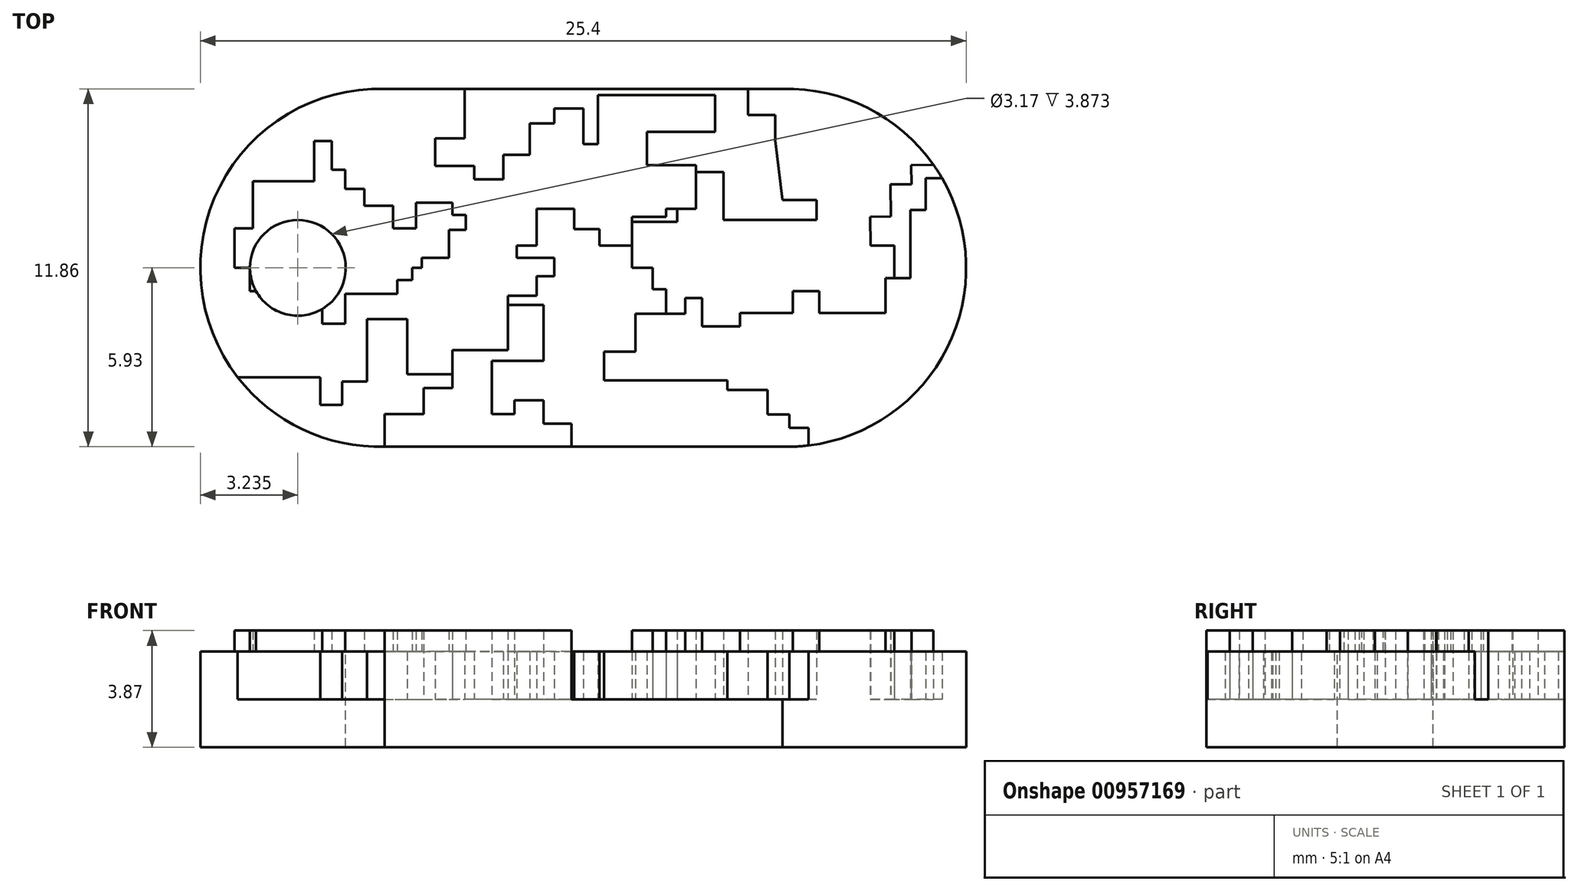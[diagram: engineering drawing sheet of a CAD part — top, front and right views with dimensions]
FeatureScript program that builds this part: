
annotation { "Feature Type Name" : "Feature", "Feature Type Description" : "" }
export const myFeature = defineFeature(function(context is Context, id is Id, definition is map)
    precondition{}
    {
        {
            var Q0;
            Q0=qCreatedBy(makeId("Top.planeOp"),FACE);
            var sketch = newSketch(context, id + "F0", { "sketchPlane" : qUnion([Q0])});
            skLineSegment(sketch, "E0.bottom", {"start": v(6.6, 5.93) * mm, "end": v(-6.6, 5.93) * mm});
            skLineSegment(sketch, "E0.top", {"start": v(6.6, -5.93) * mm, "end": v(-6.6, -5.93) * mm});
            skLineSegment(sketch, "E0.left", {"start": v(6.6, 5.93) * mm, "end": v(6.6, -5.93) * mm});
            skLineSegment(sketch, "E0.right", {"start": v(-6.6, 5.93) * mm, "end": v(-6.6, -5.93) * mm});
            skPoint(sketch, "E0.middle", {"position": v(0, 0) * mm});
            skCircle(sketch, "E1", {"center": v(6.76, 0) * mm, "radius": 5.93 * mm});
            skPoint(sketch, "E1.third.point", {"position": v(11.72, -3.25) * mm});
            skCircle(sketch, "E2", {"center": v(-6.78, 0) * mm, "radius": 5.93 * mm});
            skPoint(sketch, "E2.third.point", {"position": v(-6.95, -5.93) * mm});
            skPoint(sketch, "E3", {"position": v(-12.7, 0) * mm});
            skPoint(sketch, "E4", {"position": v(12.7, 0) * mm});
            skSolve(sketch);
        }
        {
            var Q0;
            {var subQ0=sQuery(id+"F0.wireOp",EDGE,"E0.right");Q0=makeQuery(id+"F0.imprint","IMPRINT",FACE,{"disambiguationData":[TD([[makeQuery(id+"F0.imprint","IMPRINT",EDGE,{"derivedFrom":subQ0}),-1.0]])]});}
            var Q1;
            {var subQ0=sQuery(id+"F0.wireOp",EDGE,"E0.bottom");Q1=makeQuery(id+"F0.imprint","IMPRINT",FACE,{"disambiguationData":[TD([[makeQuery(id+"F0.imprint","IMPRINT",EDGE,{"derivedFrom":subQ0}),1.0]])]});}
            var Q2;
            {var subQ0=sQuery(id+"F0.wireOp",EDGE,"E0.right");Q2=makeQuery(id+"F0.imprint","IMPRINT",FACE,{"disambiguationData":[TD([[makeQuery(id+"F0.imprint","IMPRINT",EDGE,{"derivedFrom":subQ0}),1.0]])]});}
            var Q3;
            {var subQ0=sQuery(id+"F0.wireOp",EDGE,"E0.left");Q3=makeQuery(id+"F0.imprint","IMPRINT",FACE,{"disambiguationData":[TD([[makeQuery(id+"F0.imprint","IMPRINT",EDGE,{"derivedFrom":subQ0}),-1.0]])]});}
            var Q4;
            {var subQ0=sQuery(id+"F0.wireOp",EDGE,"E0.left");Q4=makeQuery(id+"F0.imprint","IMPRINT",FACE,{"disambiguationData":[TD([[makeQuery(id+"F0.imprint","IMPRINT",EDGE,{"derivedFrom":subQ0}),1.0]])]});}
            extrude(context, id + "F1", {"entities" : qUnion([Q0, Q1, Q2, Q3, Q4]), "depth" : 1.59 * mm, "offsetDistance" : 25.4 * mm});
        }
        {
            var Q0;
            Q0=makeQuery(id+"F1.opExtrude","CAP_FACE",FACE,{"disambiguationData":[OSD([sQuery(id+"F0.wireOp",EDGE,"E0.bottom"),sQuery(id+"F0.wireOp",EDGE,"E0.top"),sQuery(id+"F0.wireOp",EDGE,"E1"),sQuery(id+"F0.wireOp",EDGE,"E2")])],"isStart":false});
            var sketch = newSketch(context, id + "F2", { "sketchPlane" : qUnion([Q0])});
            skLineSegment(sketch, "E5", {"start": v(-11.47, -3.63) * mm, "end": v(-8.73, -3.63) * mm});
            skLineSegment(sketch, "E6", {"start": v(-8.73, -3.63) * mm, "end": v(-8.73, -4.54) * mm});
            skLineSegment(sketch, "E7", {"start": v(-8.73, -4.54) * mm, "end": v(-8.01, -4.54) * mm});
            skLineSegment(sketch, "E8", {"start": v(-8.01, -4.54) * mm, "end": v(-8.01, -3.77) * mm});
            skLineSegment(sketch, "E9", {"start": v(-8.01, -3.77) * mm, "end": v(-7.18, -3.77) * mm});
            skLineSegment(sketch, "E10", {"start": v(-7.18, -3.77) * mm, "end": v(-7.18, -1.7) * mm});
            skLineSegment(sketch, "E11", {"start": v(-7.18, -1.7) * mm, "end": v(-5.84, -1.7) * mm});
            skLineSegment(sketch, "E12", {"start": v(-5.84, -1.7) * mm, "end": v(-5.84, -3.53) * mm});
            skLineSegment(sketch, "E13", {"start": v(-5.84, -3.53) * mm, "end": v(-4.35, -3.53) * mm});
            skLineSegment(sketch, "E14", {"start": v(-4.35, -3.53) * mm, "end": v(-4.35, -2.74) * mm});
            skLineSegment(sketch, "E15", {"start": v(-4.35, -2.74) * mm, "end": v(-2.5, -2.74) * mm});
            skLineSegment(sketch, "E16", {"start": v(-2.5, -2.74) * mm, "end": v(-2.5, -0.93) * mm});
            skLineSegment(sketch, "E17", {"start": v(-2.5, -0.93) * mm, "end": v(-1.55, -0.93) * mm});
            skLineSegment(sketch, "E18", {"start": v(-1.55, -0.93) * mm, "end": v(-1.55, -0.27) * mm});
            skLineSegment(sketch, "E19", {"start": v(-1.55, -0.27) * mm, "end": v(-0.97, -0.27) * mm});
            skLineSegment(sketch, "E20", {"start": v(-0.97, -0.27) * mm, "end": v(-0.97, 0.34) * mm});
            skLineSegment(sketch, "E21", {"start": v(-0.97, 0.34) * mm, "end": v(-2.2, 0.34) * mm});
            skLineSegment(sketch, "E22", {"start": v(-2.2, 0.34) * mm, "end": v(-2.2, 0.74) * mm});
            skLineSegment(sketch, "E23", {"start": v(-2.2, 0.74) * mm, "end": v(-1.55, 0.74) * mm});
            skLineSegment(sketch, "E24", {"start": v(-1.55, 0.74) * mm, "end": v(-1.55, 1.96) * mm});
            skLineSegment(sketch, "E25", {"start": v(-1.55, 1.96) * mm, "end": v(-0.31, 1.96) * mm});
            skLineSegment(sketch, "E26", {"start": v(-0.31, 1.96) * mm, "end": v(-0.31, 1.28) * mm});
            skLineSegment(sketch, "E27", {"start": v(-0.31, 1.28) * mm, "end": v(0.52, 1.28) * mm});
            skLineSegment(sketch, "E28", {"start": v(0.52, 1.28) * mm, "end": v(0.52, 0.74) * mm});
            skLineSegment(sketch, "E29", {"start": v(0.52, 0.74) * mm, "end": v(1.6, 0.74) * mm});
            skLineSegment(sketch, "E30", {"start": v(1.6, 0.74) * mm, "end": v(1.6, 1.7) * mm});
            skLineSegment(sketch, "E31", {"start": v(1.6, 1.7) * mm, "end": v(2.74, 1.7) * mm});
            skLineSegment(sketch, "E32", {"start": v(2.74, 1.7) * mm, "end": v(2.74, 1.96) * mm});
            skLineSegment(sketch, "E33", {"start": v(2.74, 1.96) * mm, "end": v(3.73, 1.96) * mm});
            skLineSegment(sketch, "E34", {"start": v(3.73, 1.96) * mm, "end": v(3.73, 3.4) * mm});
            skLineSegment(sketch, "E35", {"start": v(3.73, 3.4) * mm, "end": v(2.1, 3.4) * mm});
            skLineSegment(sketch, "E36", {"start": v(2.1, 3.4) * mm, "end": v(2.1, 4.51) * mm});
            skLineSegment(sketch, "E37", {"start": v(2.1, 4.51) * mm, "end": v(4.36, 4.51) * mm});
            skLineSegment(sketch, "E38", {"start": v(4.36, 4.51) * mm, "end": v(4.36, 5.73) * mm});
            skLineSegment(sketch, "E39", {"start": v(4.36, 5.73) * mm, "end": v(0.48, 5.73) * mm});
            skLineSegment(sketch, "E40", {"start": v(0.48, 5.73) * mm, "end": v(0.48, 4.1) * mm});
            skLineSegment(sketch, "E41", {"start": v(0.48, 4.1) * mm, "end": v(0, 4.1) * mm});
            skLineSegment(sketch, "E42", {"start": v(0, 4.1) * mm, "end": v(0, 5.28) * mm});
            skLineSegment(sketch, "E43", {"start": v(0, 5.28) * mm, "end": v(-0.97, 5.28) * mm});
            skLineSegment(sketch, "E44", {"start": v(-0.97, 5.28) * mm, "end": v(-0.97, 4.78) * mm});
            skLineSegment(sketch, "E45", {"start": v(-0.97, 4.78) * mm, "end": v(-1.78, 4.78) * mm});
            skLineSegment(sketch, "E46", {"start": v(-1.78, 4.78) * mm, "end": v(-1.78, 3.75) * mm});
            skLineSegment(sketch, "E47", {"start": v(-1.78, 3.75) * mm, "end": v(-2.66, 3.75) * mm});
            skLineSegment(sketch, "E48", {"start": v(-2.66, 3.75) * mm, "end": v(-2.66, 2.93) * mm});
            skLineSegment(sketch, "E49", {"start": v(-2.66, 2.93) * mm, "end": v(-3.63, 2.93) * mm});
            skLineSegment(sketch, "E50", {"start": v(-3.63, 2.93) * mm, "end": v(-3.63, 3.38) * mm});
            skLineSegment(sketch, "E51", {"start": v(-3.63, 3.38) * mm, "end": v(-4.92, 3.38) * mm});
            skLineSegment(sketch, "E52", {"start": v(-4.92, 3.38) * mm, "end": v(-4.92, 4.29) * mm});
            skLineSegment(sketch, "E53", {"start": v(-4.92, 4.29) * mm, "end": v(-3.95, 4.29) * mm});
            skLineSegment(sketch, "E54", {"start": v(-3.95, 4.29) * mm, "end": v(-3.95, 5.93) * mm});
            skLineSegment(sketch, "E55", {"start": v(-10.88, -0.77) * mm, "end": v(-9.98, -0.77) * mm});
            skLineSegment(sketch, "E56", {"start": v(-9.98, -0.77) * mm, "end": v(-9.98, -1.27) * mm});
            skLineSegment(sketch, "E57", {"start": v(-9.98, -1.27) * mm, "end": v(-8.67, -1.27) * mm});
            skLineSegment(sketch, "E58", {"start": v(-8.67, -1.27) * mm, "end": v(-8.67, -1.86) * mm});
            skLineSegment(sketch, "E59", {"start": v(-8.67, -1.86) * mm, "end": v(-7.9, -1.86) * mm});
            skLineSegment(sketch, "E60", {"start": v(-7.9, -1.86) * mm, "end": v(-7.9, -0.86) * mm});
            skLineSegment(sketch, "E61", {"start": v(-7.9, -0.86) * mm, "end": v(-6.18, -0.86) * mm});
            skLineSegment(sketch, "E62", {"start": v(-6.18, -0.86) * mm, "end": v(-6.18, -0.4) * mm});
            skLineSegment(sketch, "E63", {"start": v(-6.18, -0.4) * mm, "end": v(-5.69, -0.4) * mm});
            skLineSegment(sketch, "E64", {"start": v(-5.69, -0.4) * mm, "end": v(-5.69, 0) * mm});
            skLineSegment(sketch, "E65", {"start": v(-5.69, 0) * mm, "end": v(-5.37, 0) * mm});
            skLineSegment(sketch, "E66", {"start": v(-5.37, 0) * mm, "end": v(-5.37, 0.34) * mm});
            skLineSegment(sketch, "E67", {"start": v(-5.37, 0.34) * mm, "end": v(-4.47, 0.34) * mm});
            skLineSegment(sketch, "E68", {"start": v(-4.47, 0.34) * mm, "end": v(-4.47, 1.26) * mm});
            skLineSegment(sketch, "E69", {"start": v(-4.47, 1.26) * mm, "end": v(-3.9, 1.26) * mm});
            skLineSegment(sketch, "E70", {"start": v(-3.9, 1.26) * mm, "end": v(-3.9, 1.76) * mm});
            skLineSegment(sketch, "E71", {"start": v(-3.9, 1.76) * mm, "end": v(-4.35, 1.76) * mm});
            skLineSegment(sketch, "E72", {"start": v(-4.35, 1.76) * mm, "end": v(-4.35, 2.16) * mm});
            skLineSegment(sketch, "E73", {"start": v(-4.35, 2.16) * mm, "end": v(-5.55, 2.16) * mm});
            skLineSegment(sketch, "E74", {"start": v(-5.55, 2.16) * mm, "end": v(-5.55, 1.3) * mm});
            skLineSegment(sketch, "E75", {"start": v(-5.55, 1.3) * mm, "end": v(-6.32, 1.3) * mm});
            skLineSegment(sketch, "E76", {"start": v(-6.32, 1.3) * mm, "end": v(-6.32, 2.05) * mm});
            skLineSegment(sketch, "E77", {"start": v(-6.32, 2.05) * mm, "end": v(-7.27, 2.05) * mm});
            skLineSegment(sketch, "E78", {"start": v(-7.27, 2.05) * mm, "end": v(-7.27, 2.62) * mm});
            skLineSegment(sketch, "E79", {"start": v(-7.27, 2.62) * mm, "end": v(-7.9, 2.62) * mm});
            skLineSegment(sketch, "E80", {"start": v(-7.9, 2.62) * mm, "end": v(-7.9, 3.25) * mm});
            skLineSegment(sketch, "E81", {"start": v(-7.9, 3.25) * mm, "end": v(-8.35, 3.25) * mm});
            skLineSegment(sketch, "E82", {"start": v(-8.35, 3.25) * mm, "end": v(-8.35, 4.2) * mm});
            skLineSegment(sketch, "E83", {"start": v(-8.35, 4.2) * mm, "end": v(-8.94, 4.2) * mm});
            skLineSegment(sketch, "E84", {"start": v(-8.94, 4.2) * mm, "end": v(-8.94, 2.87) * mm});
            skLineSegment(sketch, "E85", {"start": v(-8.94, 2.87) * mm, "end": v(-10.97, 2.87) * mm});
            skLineSegment(sketch, "E86", {"start": v(-10.97, 2.87) * mm, "end": v(-10.97, 1.3) * mm});
            skLineSegment(sketch, "E87", {"start": v(-10.97, 1.3) * mm, "end": v(-11.58, 1.3) * mm});
            skLineSegment(sketch, "E88", {"start": v(-11.58, 1.3) * mm, "end": v(-11.58, 0) * mm});
            skLineSegment(sketch, "E89", {"start": v(-11.58, 0) * mm, "end": v(-11.06, 0) * mm});
            skLineSegment(sketch, "E90", {"start": v(-11.06, 0) * mm, "end": v(-11.06, -0.77) * mm});
            skLineSegment(sketch, "E91", {"start": v(-11.06, -0.77) * mm, "end": v(-10.88, -0.77) * mm});
            skLineSegment(sketch, "E92", {"start": v(11.9, 2.97) * mm, "end": v(11.35, 2.97) * mm});
            skLineSegment(sketch, "E93", {"start": v(11.35, 2.97) * mm, "end": v(11.35, 1.92) * mm});
            skLineSegment(sketch, "E94", {"start": v(11.35, 1.92) * mm, "end": v(10.84, 1.92) * mm});
            skLineSegment(sketch, "E95", {"start": v(10.84, 1.92) * mm, "end": v(10.84, -0.35) * mm});
            skLineSegment(sketch, "E96", {"start": v(10.84, -0.35) * mm, "end": v(10.02, -0.35) * mm});
            skLineSegment(sketch, "E97", {"start": v(10.02, -0.35) * mm, "end": v(10.02, -1.5) * mm});
            skLineSegment(sketch, "E98", {"start": v(10.02, -1.5) * mm, "end": v(7.82, -1.5) * mm});
            skLineSegment(sketch, "E99", {"start": v(7.82, -1.5) * mm, "end": v(7.82, -0.77) * mm});
            skLineSegment(sketch, "E100", {"start": v(7.82, -0.77) * mm, "end": v(6.95, -0.77) * mm});
            skLineSegment(sketch, "E101", {"start": v(6.95, -0.77) * mm, "end": v(6.95, -1.5) * mm});
            skLineSegment(sketch, "E102", {"start": v(6.95, -1.5) * mm, "end": v(5.19, -1.5) * mm});
            skLineSegment(sketch, "E103", {"start": v(5.19, -1.5) * mm, "end": v(5.19, -1.94) * mm});
            skLineSegment(sketch, "E104", {"start": v(5.19, -1.94) * mm, "end": v(3.93, -1.94) * mm});
            skLineSegment(sketch, "E105", {"start": v(3.93, -1.94) * mm, "end": v(3.93, -1) * mm});
            skLineSegment(sketch, "E106", {"start": v(3.93, -1) * mm, "end": v(3.37, -1) * mm});
            skLineSegment(sketch, "E107", {"start": v(3.37, -1) * mm, "end": v(3.37, -1.52) * mm});
            skLineSegment(sketch, "E108", {"start": v(3.37, -1.52) * mm, "end": v(1.72, -1.52) * mm});
            skLineSegment(sketch, "E109", {"start": v(1.72, -1.52) * mm, "end": v(1.72, -2.78) * mm});
            skLineSegment(sketch, "E110", {"start": v(1.72, -2.78) * mm, "end": v(0.69, -2.78) * mm});
            skLineSegment(sketch, "E111", {"start": v(0.69, -2.78) * mm, "end": v(0.69, -3.73) * mm});
            skLineSegment(sketch, "E112", {"start": v(0.69, -3.73) * mm, "end": v(4.77, -3.73) * mm});
            skLineSegment(sketch, "E113", {"start": v(4.77, -3.73) * mm, "end": v(4.77, -4.05) * mm});
            skLineSegment(sketch, "E114", {"start": v(4.77, -4.05) * mm, "end": v(6.1, -4.05) * mm});
            skLineSegment(sketch, "E115", {"start": v(6.1, -4.05) * mm, "end": v(6.1, -4.86) * mm});
            skLineSegment(sketch, "E116", {"start": v(6.1, -4.86) * mm, "end": v(6.83, -4.86) * mm});
            skLineSegment(sketch, "E117", {"start": v(6.83, -4.86) * mm, "end": v(6.83, -5.31) * mm});
            skLineSegment(sketch, "E118", {"start": v(6.83, -5.31) * mm, "end": v(7.46, -5.31) * mm});
            skLineSegment(sketch, "E119", {"start": v(7.46, -5.31) * mm, "end": v(7.46, -5.93) * mm});
            skSolve(sketch);
        }
        {
            var Q0;
            {var subQ3=sQuery(id+"F2.wireOp",EDGE,"E5");Q0=makeQuery(id+"F2.imprint","IMPRINT",FACE,{"disambiguationData":[TD([[makeQuery(id+"F2.imprint","IMPRINT",EDGE,{"derivedFrom":subQ3}),1.0]])]});}
            var Q1;
            {var subQ0=sQuery(id+"F2.wireOp",EDGE,"E92");Q1=makeQuery(id+"F2.imprint","IMPRINT",FACE,{"disambiguationData":[TD([[makeQuery(id+"F2.imprint","IMPRINT",EDGE,{"derivedFrom":subQ0}),1.0]])]});}
            extrude(context, id + "F3", {"entities" : qUnion([Q0, Q1]), "operationType" : NewBodyOperationType.ADD, "depth" : 1.59 * mm, "offsetDistance" : 25.4 * mm});
        }
        {
            var Q0;
            {var subQ0=sQuery(id+"F0.wireOp",EDGE,"E0.bottom");var subQ1=sQuery(id+"F0.wireOp",EDGE,"E2");var subQ2=sQuery(id+"F0.wireOp",EDGE,"E1");var subQ3=sQuery(id+"F0.wireOp",EDGE,"E0.top");Q0=makeQuery(id+"F3.boolean.opBoolean","SPLIT",FACE,{"disambiguationData":[TD([makeQuery(id+"F1.opExtrude","SWEPT_FACE",FACE,{"disambiguationData":[OSD([subQ0])]})])],"derivedFrom":makeQuery(id+"F1.opExtrude","CAP_FACE",FACE,{"disambiguationData":[OSD([subQ0,subQ3,subQ2,subQ1])],"isStart":false})});}
            var sketch = newSketch(context, id + "F4", { "sketchPlane" : qUnion([Q0])});
            skLineSegment(sketch, "E120", {"start": v(-6.6, -5.93) * mm, "end": v(-6.6, -4.85) * mm});
            skLineSegment(sketch, "E121", {"start": v(-6.6, -4.85) * mm, "end": v(-5.3, -4.85) * mm});
            skLineSegment(sketch, "E122", {"start": v(-5.3, -4.85) * mm, "end": v(-5.3, -3.99) * mm});
            skLineSegment(sketch, "E123", {"start": v(-5.3, -3.99) * mm, "end": v(-4.35, -3.99) * mm});
            skLineSegment(sketch, "E124", {"start": v(-4.35, -3.99) * mm, "end": v(-4.35, -2.05) * mm});
            skLineSegment(sketch, "E125", {"start": v(-4.35, -2.05) * mm, "end": v(-2.5, -2.05) * mm});
            skLineSegment(sketch, "E126", {"start": v(-2.5, -2.05) * mm, "end": v(-2.5, -1.23) * mm});
            skLineSegment(sketch, "E127", {"start": v(-2.5, -1.23) * mm, "end": v(-1.33, -1.23) * mm});
            skLineSegment(sketch, "E128", {"start": v(-1.33, -1.23) * mm, "end": v(-1.33, -3.09) * mm});
            skLineSegment(sketch, "E129", {"start": v(-1.33, -3.09) * mm, "end": v(-3.04, -3.09) * mm});
            skLineSegment(sketch, "E130", {"start": v(-3.04, -3.09) * mm, "end": v(-3.04, -4.85) * mm});
            skLineSegment(sketch, "E131", {"start": v(-3.04, -4.85) * mm, "end": v(-2.3, -4.85) * mm});
            skLineSegment(sketch, "E132", {"start": v(-2.3, -4.85) * mm, "end": v(-2.3, -4.4) * mm});
            skLineSegment(sketch, "E133", {"start": v(-2.3, -4.4) * mm, "end": v(-1.33, -4.4) * mm});
            skLineSegment(sketch, "E134", {"start": v(-1.33, -4.4) * mm, "end": v(-1.33, -5.16) * mm});
            skLineSegment(sketch, "E135", {"start": v(-1.33, -5.16) * mm, "end": v(-0.4, -5.16) * mm});
            skLineSegment(sketch, "E136", {"start": v(-0.4, -5.16) * mm, "end": v(-0.4, -5.93) * mm});
            skLineSegment(sketch, "E137", {"start": v(5.45, 5.93) * mm, "end": v(5.45, 5.07) * mm});
            skLineSegment(sketch, "E138", {"start": v(5.45, 5.07) * mm, "end": v(6.35, 5.07) * mm});
            skLineSegment(sketch, "E139", {"start": v(6.35, 5.07) * mm, "end": v(6.35, 4.23) * mm});
            skLineSegment(sketch, "E140", {"start": v(6.35, 4.23) * mm, "end": v(6.6, 2.24) * mm});
            skLineSegment(sketch, "E141", {"start": v(6.6, 2.24) * mm, "end": v(7.73, 2.24) * mm});
            skLineSegment(sketch, "E142", {"start": v(7.73, 2.24) * mm, "end": v(7.73, 1.59) * mm});
            skLineSegment(sketch, "E143", {"start": v(7.73, 1.59) * mm, "end": v(4.64, 1.59) * mm});
            skLineSegment(sketch, "E144", {"start": v(4.64, 1.59) * mm, "end": v(4.64, 3.17) * mm});
            skLineSegment(sketch, "E145", {"start": v(4.64, 3.17) * mm, "end": v(3.1, 3.17) * mm});
            skLineSegment(sketch, "E146", {"start": v(3.1, 3.17) * mm, "end": v(3.1, 1.52) * mm});
            skLineSegment(sketch, "E147", {"start": v(3.1, 1.52) * mm, "end": v(1.6, 1.52) * mm});
            skLineSegment(sketch, "E148", {"start": v(1.6, 1.52) * mm, "end": v(1.6, 0) * mm});
            skLineSegment(sketch, "E149", {"start": v(1.6, 0) * mm, "end": v(2.29, 0) * mm});
            skLineSegment(sketch, "E150", {"start": v(2.29, 0) * mm, "end": v(2.29, -0.72) * mm});
            skLineSegment(sketch, "E151", {"start": v(2.29, -0.72) * mm, "end": v(2.74, -0.72) * mm});
            skLineSegment(sketch, "E152", {"start": v(2.74, -0.72) * mm, "end": v(2.74, -2.02) * mm});
            skLineSegment(sketch, "E153", {"start": v(2.74, -2.02) * mm, "end": v(10.33, -1.94) * mm});
            skLineSegment(sketch, "E154", {"start": v(10.33, -1.94) * mm, "end": v(10.3, 0.74) * mm});
            skLineSegment(sketch, "E155", {"start": v(10.3, 0.74) * mm, "end": v(9.52, 0.73) * mm});
            skLineSegment(sketch, "E156", {"start": v(9.52, 0.73) * mm, "end": v(9.5, 1.7) * mm});
            skLineSegment(sketch, "E157", {"start": v(9.5, 1.7) * mm, "end": v(10.2, 1.7) * mm});
            skLineSegment(sketch, "E158", {"start": v(10.2, 1.7) * mm, "end": v(10.18, 2.76) * mm});
            skLineSegment(sketch, "E159", {"start": v(10.18, 2.76) * mm, "end": v(10.87, 2.77) * mm});
            skLineSegment(sketch, "E160", {"start": v(10.87, 2.77) * mm, "end": v(10.87, 3.4) * mm});
            skLineSegment(sketch, "E161", {"start": v(10.87, 3.4) * mm, "end": v(11.6, 3.42) * mm});
            skLineSegment(sketch, "E162", {"start": v(-4.22, -0.44) * mm, "end": v(-3.31, -0.44) * mm});
            skLineSegment(sketch, "E163", {"start": v(-3.31, -0.44) * mm, "end": v(-3.31, 0.35) * mm});
            skLineSegment(sketch, "E164", {"start": v(-3.31, 0.35) * mm, "end": v(-2.75, 0.35) * mm});
            skLineSegment(sketch, "E165", {"start": v(-2.75, 0.35) * mm, "end": v(-2.75, 1) * mm});
            skLineSegment(sketch, "E166", {"start": v(-2.75, 1) * mm, "end": v(-4, 1) * mm});
            skLineSegment(sketch, "E167", {"start": v(-4, 1) * mm, "end": v(-4, 0) * mm});
            skLineSegment(sketch, "E168", {"start": v(-4, 0) * mm, "end": v(-4.22, 0) * mm});
            skLineSegment(sketch, "E169", {"start": v(-4.22, 0) * mm, "end": v(-4.22, -0.44) * mm});
            skSolve(sketch);
        }
        {
            var Q0;
            {var subQ5=sQuery(id+"F4.wireOp",EDGE,"E120");Q0=makeQuery(id+"F4.imprint","IMPRINT",FACE,{"disambiguationData":[TD([[makeQuery(id+"F4.imprint","IMPRINT",EDGE,{"derivedFrom":subQ5}),-1.0]])]});}
            var Q1;
            {var subQ17=sQuery(id+"F4.wireOp",EDGE,"E137");Q1=makeQuery(id+"F4.imprint","IMPRINT",FACE,{"disambiguationData":[TD([[makeQuery(id+"F4.imprint","IMPRINT",EDGE,{"derivedFrom":subQ17}),1.0]])]});}
            var Q2;
            Q2=makeQuery(id+"F2.imprint","IMPRINT",FACE,{"disambiguationData":[TD([[makeQuery(id+"F2.imprint","IMPRINT",EDGE,{"derivedFrom":sQuery(id+"F2.wireOp",EDGE,"E55")}),1.0]])]});
            extrude(context, id + "F5", {"entities" : qUnion([Q0, Q1, Q2]), "operationType" : NewBodyOperationType.ADD, "depth" : 2.3 * mm, "offsetDistance" : 25.4 * mm});
        }
        {
            var Q0;
            Q0=makeQuery(id+"F5.opExtrude","CAP_FACE",FACE,{"disambiguationData":[OSD([sQuery(id+"F2.wireOp",EDGE,"E55"),sQuery(id+"F2.wireOp",EDGE,"E56"),sQuery(id+"F2.wireOp",EDGE,"E57"),sQuery(id+"F2.wireOp",EDGE,"E58"),sQuery(id+"F2.wireOp",EDGE,"E59"),sQuery(id+"F2.wireOp",EDGE,"E60"),sQuery(id+"F2.wireOp",EDGE,"E61"),sQuery(id+"F2.wireOp",EDGE,"E62"),sQuery(id+"F2.wireOp",EDGE,"E63"),sQuery(id+"F2.wireOp",EDGE,"E64"),sQuery(id+"F2.wireOp",EDGE,"E65"),sQuery(id+"F2.wireOp",EDGE,"E66"),sQuery(id+"F2.wireOp",EDGE,"E67"),sQuery(id+"F2.wireOp",EDGE,"E68"),sQuery(id+"F2.wireOp",EDGE,"E69"),sQuery(id+"F2.wireOp",EDGE,"E70"),sQuery(id+"F2.wireOp",EDGE,"E71"),sQuery(id+"F2.wireOp",EDGE,"E72"),sQuery(id+"F2.wireOp",EDGE,"E73"),sQuery(id+"F2.wireOp",EDGE,"E74"),sQuery(id+"F2.wireOp",EDGE,"E75"),sQuery(id+"F2.wireOp",EDGE,"E76"),sQuery(id+"F2.wireOp",EDGE,"E77"),sQuery(id+"F2.wireOp",EDGE,"E78"),sQuery(id+"F2.wireOp",EDGE,"E79"),sQuery(id+"F2.wireOp",EDGE,"E80"),sQuery(id+"F2.wireOp",EDGE,"E81"),sQuery(id+"F2.wireOp",EDGE,"E82"),sQuery(id+"F2.wireOp",EDGE,"E83"),sQuery(id+"F2.wireOp",EDGE,"E84"),sQuery(id+"F2.wireOp",EDGE,"E85"),sQuery(id+"F2.wireOp",EDGE,"E86"),sQuery(id+"F2.wireOp",EDGE,"E87"),sQuery(id+"F2.wireOp",EDGE,"E88"),sQuery(id+"F2.wireOp",EDGE,"E89"),sQuery(id+"F2.wireOp",EDGE,"E90"),sQuery(id+"F2.wireOp",EDGE,"E91")])],"isStart":false});
            var sketch = newSketch(context, id + "F6", { "sketchPlane" : qUnion([Q0])});
            skPoint(sketch, "E170", {"position": v(-9.48, 0) * mm});
            skSolve(sketch);
        }
        {
            var Q0;
            Q0=sQuery(id+"F6.wireOp",VERTEX,"E170");
            var Q1;
            Q1=makeQuery(id+"F1.opExtrude","SWEPT_BODY",BODY,{"disambiguationData":[OSD([sQuery(id+"F0.wireOp",EDGE,"E0.bottom"),sQuery(id+"F0.wireOp",EDGE,"E0.top"),sQuery(id+"F0.wireOp",EDGE,"E1"),sQuery(id+"F0.wireOp",EDGE,"E2")])]});
            hole(context, id + "F7", {"style" : HoleStyle.SIMPLE, "endStyle" : HoleEndStyle.THROUGH, "holeDiameter" : 3.17 * mm, "majorDiameter" : 6.35 * mm, "isTappedThrough" : true, "tappedDepth" : 12.7 * mm, "tapClearance" : 3, "locations" : qUnion([Q0]), "scope" : qUnion([Q1])});
        }
    });
